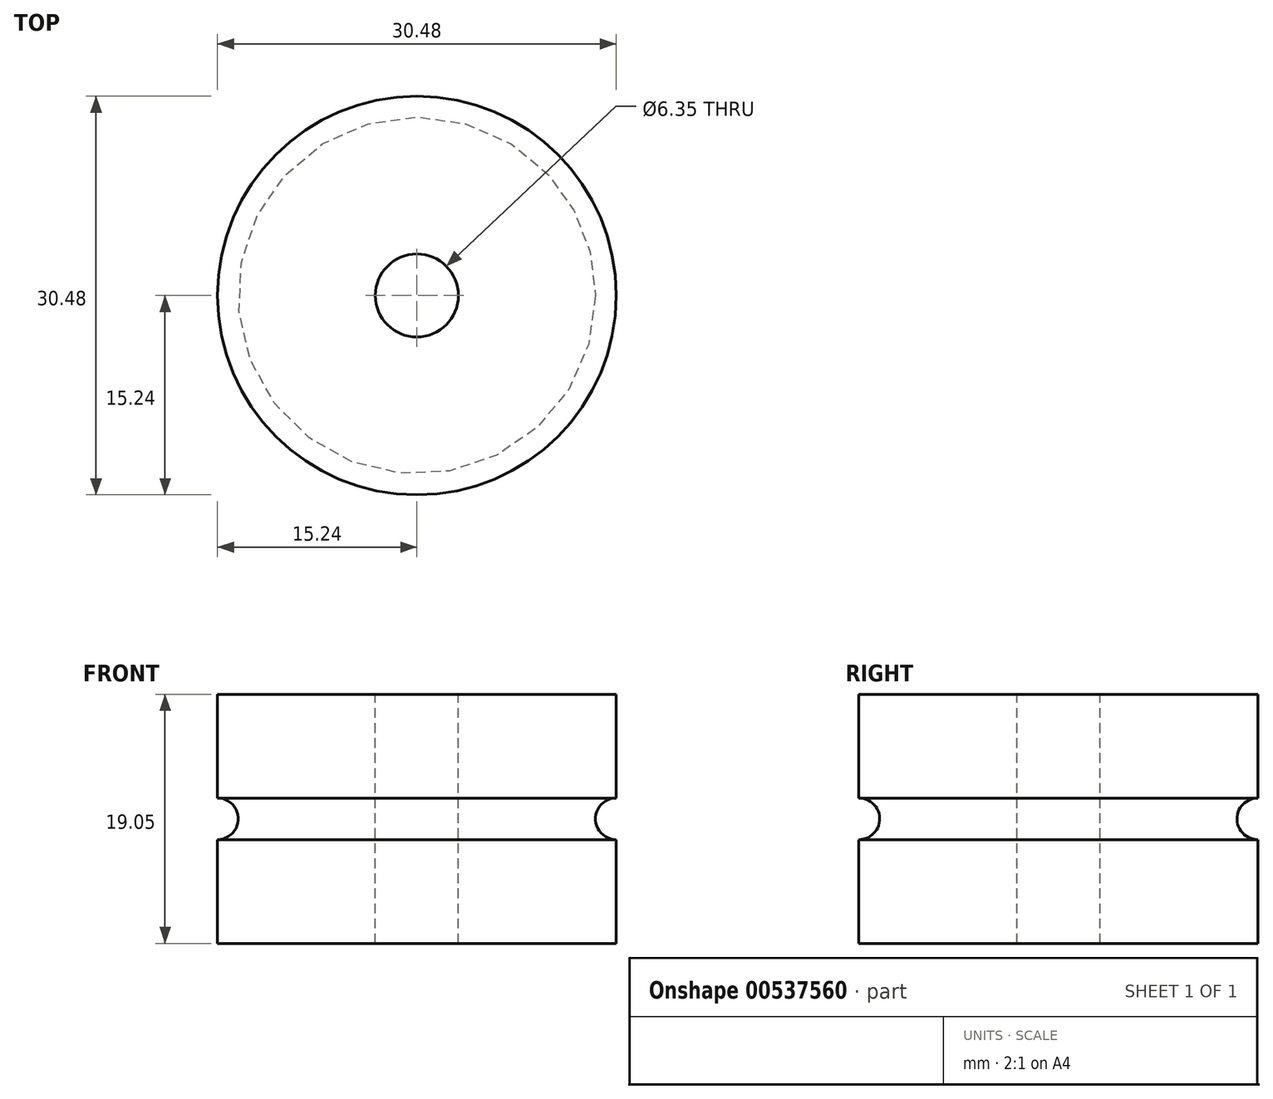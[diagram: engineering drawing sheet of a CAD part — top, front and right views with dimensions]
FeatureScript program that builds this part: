
annotation { "Feature Type Name" : "Feature", "Feature Type Description" : "" }
export const myFeature = defineFeature(function(context is Context, id is Id, definition is map)
    precondition{}
    {
        {
            var Q0;
            Q0=qCreatedBy(makeId("Front.planeOp"),FACE);
            var sketch = newSketch(context, id + "F0", { "sketchPlane" : qUnion([Q0])});
            skLineSegment(sketch, "E0.bottom", {"start": v(0, 0) * mm, "end": v(-15.24, 0) * mm});
            skLineSegment(sketch, "E0.top", {"start": v(0, -19.05) * mm, "end": v(-15.24, -19.05) * mm});
            skLineSegment(sketch, "E0.left", {"start": v(0, 0) * mm, "end": v(0, -19.05) * mm});
            skLineSegment(sketch, "E0.right", {"start": v(-15.24, 0) * mm, "end": v(-15.24, -19.05) * mm});
            skCircle(sketch, "E1", {"center": v(-15.24, -9.53) * mm, "radius": 1.59 * mm});
            skSolve(sketch);
        }
        {
            var Q0;
            {var subQ1=sQuery(id+"F0.wireOp",EDGE,"E0.bottom");Q0=makeQuery(id+"F0.imprint","IMPRINT",FACE,{"disambiguationData":[TD([[makeQuery(id+"F0.imprint","IMPRINT",EDGE,{"derivedFrom":subQ1}),1.0]])]});}
            var Q1;
            Q1=sQuery(id+"F0.wireOp",EDGE,"E0.left");
            revolve(context, id + "F1", {"entities" : qUnion([Q0]), "axis" : qUnion([Q1]), "revolveType" : RevolveType.FULL});
        }
        {
            var Q0;
            Q0=makeQuery(id+"F1.opRevolve","SWEPT_FACE",FACE,{"disambiguationData":[OSD([sQuery(id+"F0.wireOp",EDGE,"E0.bottom")])]});
            var sketch = newSketch(context, id + "F2", { "sketchPlane" : qUnion([Q0])});
            skCircle(sketch, "E2", {"center": v(0, 0) * mm, "radius": 3.18 * mm});
            skSolve(sketch);
        }
        {
            var Q0;
            Q0=makeQuery(id+"F2.imprint","IMPRINT",FACE,{"disambiguationData":[TD([[makeQuery(id+"F2.imprint","IMPRINT",EDGE,{"derivedFrom":sQuery(id+"F2.wireOp",EDGE,"E2")}),1.0]])]});
            extrude(context, id + "F3", {"entities" : qUnion([Q0]), "operationType" : NewBodyOperationType.REMOVE, "oppositeDirection" : true, "depth" : 25.4 * mm, "offsetDistance" : 25.4 * mm});
        }
        {
            var Q0;
            Q0=makeQuery(id+"F1.opRevolve","SWEPT_FACE",FACE,{"disambiguationData":[OSD([sQuery(id+"F0.wireOp",EDGE,"E0.bottom")])]});
            var sketch = newSketch(context, id + "F4", { "sketchPlane" : qUnion([Q0])});
            skCircle(sketch, "E3", {"center": v(0, 0) * mm, "radius": 3.18 * mm});
            skSolve(sketch);
        }
        {
            var Q0;
            Q0=makeQuery(id+"F4.imprint","IMPRINT",FACE,{"disambiguationData":[TD([[makeQuery(id+"F4.imprint","IMPRINT",EDGE,{"derivedFrom":sQuery(id+"F4.wireOp",EDGE,"E3")}),1.0]])]});
            extrude(context, id + "F5", {"entities" : qUnion([Q0]), "operationType" : NewBodyOperationType.REMOVE, "oppositeDirection" : true, "depth" : 25.4 * mm, "offsetDistance" : 25.4 * mm});
        }
    });
